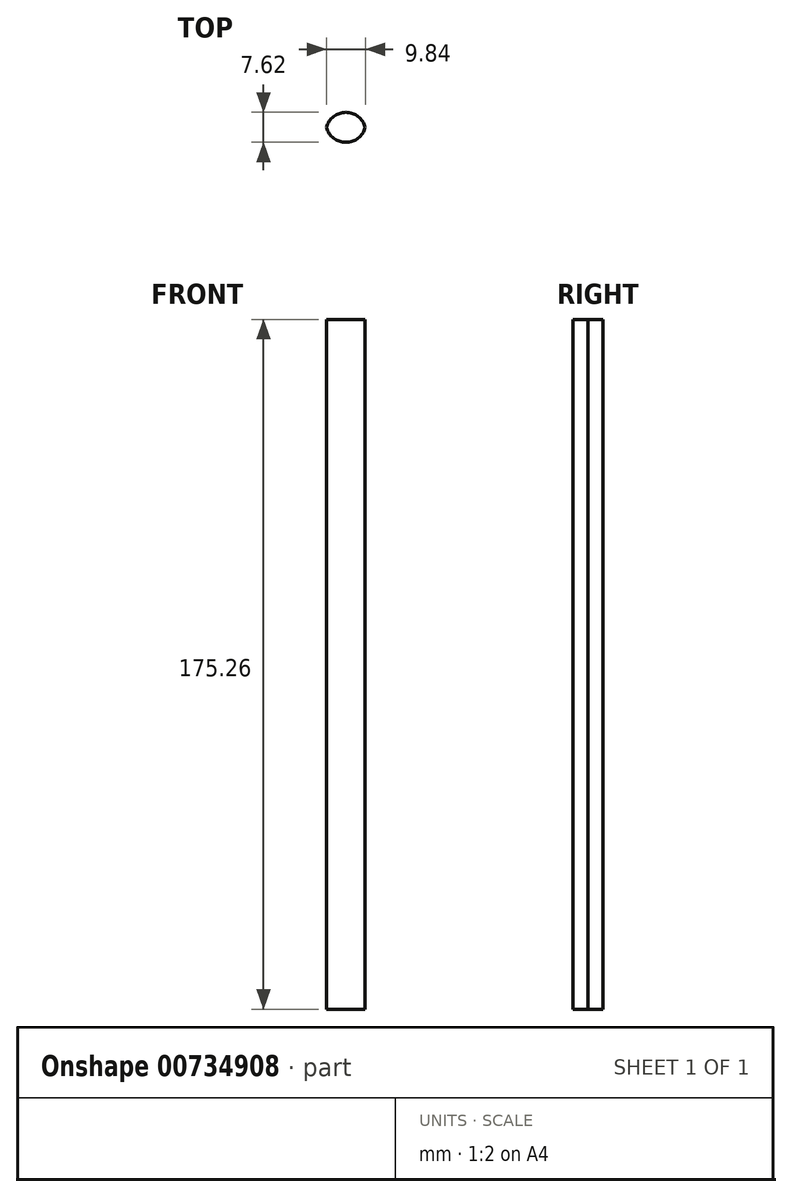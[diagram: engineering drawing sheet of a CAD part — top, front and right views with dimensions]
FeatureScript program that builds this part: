
annotation { "Feature Type Name" : "Feature", "Feature Type Description" : "" }
export const myFeature = defineFeature(function(context is Context, id is Id, definition is map)
    precondition{}
    {
        {
            var Q0;
            Q0=qCreatedBy(makeId("Front.planeOp"),FACE);
            var sketch = newSketch(context, id + "F0", { "sketchPlane" : qUnion([Q0])});
            skLineSegment(sketch, "E0", {"start": v(0, 77.72) * mm, "end": v(0, -72.14) * mm});
            skLineSegment(sketch, "E1", {"start": v(0, -72.14) * mm, "end": v(0, -97.54) * mm});
            skLineSegment(sketch, "E2", {"start": v(0, 77.72) * mm, "end": v(10.16, 77.72) * mm});
            skLineSegment(sketch, "E3", {"start": v(10.16, 77.72) * mm, "end": v(10.16, -97.54) * mm});
            skLineSegment(sketch, "E4", {"start": v(10.16, -97.54) * mm, "end": v(0, -97.54) * mm});
            skSolve(sketch);
        }
        {
            var Q0;
            Q0=makeQuery(id+"F0.imprint","IMPRINT",FACE,{"disambiguationData":[TD([[makeQuery(id+"F0.imprint","IMPRINT",EDGE,{"derivedFrom":sQuery(id+"F0.wireOp",EDGE,"E0")}),1.0]])]});
            extrude(context, id + "F1", {"entities" : qUnion([Q0]), "depth" : 7.62 * mm, "offsetDistance" : 25.4 * mm});
        }
        {
            var Q0;
            Q0=makeQuery(id+"F1.opExtrude","CAP_EDGE",EDGE,{"disambiguationData":[OSD([sQuery(id+"F0.wireOp",EDGE,"E3")])],"isStart":false});
            var Q1;
            Q1=makeQuery(id+"F1.opExtrude","CAP_EDGE",EDGE,{"disambiguationData":[OSD([sQuery(id+"F0.wireOp",EDGE,"E3")])],"isStart":true});
            var Q2;
            Q2=makeQuery(id+"F1.opExtrude","CAP_EDGE",EDGE,{"disambiguationData":[OSD([sQuery(id+"F0.wireOp",EDGE,"E0"),sQuery(id+"F0.wireOp",EDGE,"E1")])],"isStart":false});
            var Q3;
            Q3=makeQuery(id+"F1.opExtrude","CAP_EDGE",EDGE,{"disambiguationData":[OSD([sQuery(id+"F0.wireOp",EDGE,"E0"),sQuery(id+"F0.wireOp",EDGE,"E1")])],"isStart":true});
            fillet(context, id + "F2", {"entities" : qUnion([Q0, Q1, Q2, Q3]), "radius" : 5.08 * mm, "tangentPropagation" : true, "allowEdgeOverflow" : false});
        }
    });
